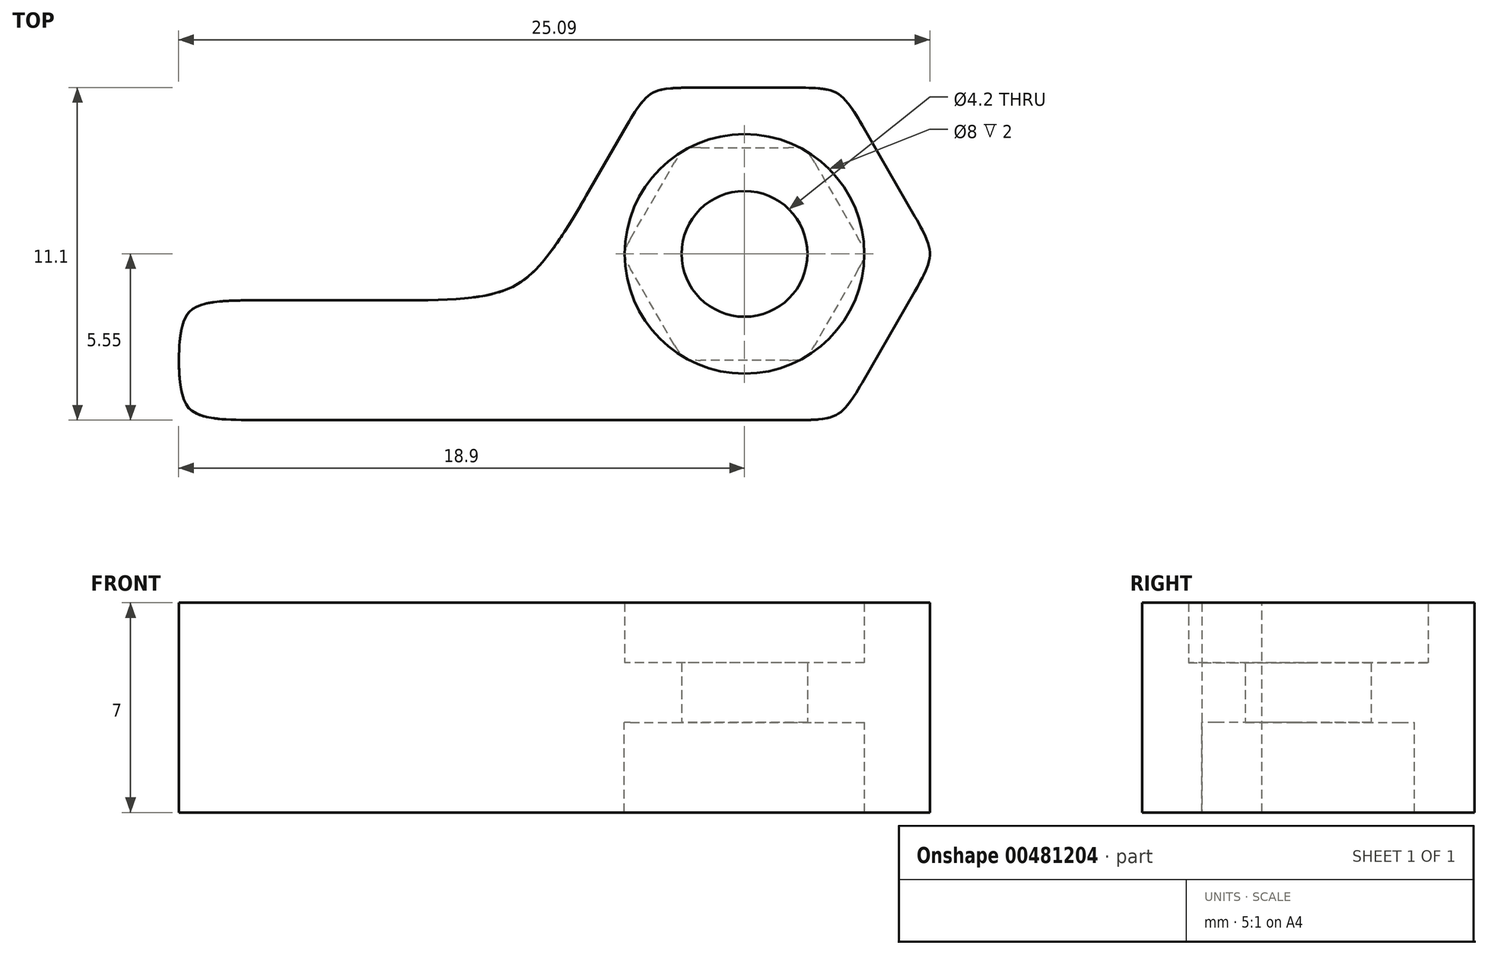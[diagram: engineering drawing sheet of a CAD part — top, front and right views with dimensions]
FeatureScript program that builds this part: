
annotation { "Feature Type Name" : "Feature", "Feature Type Description" : "" }
export const myFeature = defineFeature(function(context is Context, id is Id, definition is map)
    precondition{}
    {
        {
            var Q0;
            Q0=qCreatedBy(makeId("Top.planeOp"),FACE);
            var sketch = newSketch(context, id + "F0", { "sketchPlane" : qUnion([Q0])});
            skCircle(sketch, "E0", {"center": v(0, 0) * mm, "radius": 3.55 * mm, "construction": true});
            skLineSegment(sketch, "E1", {"start": v(-2.05, 3.55) * mm, "end": v(2.05, 3.55) * mm});
            skLineSegment(sketch, "E2", {"start": v(2.05, 3.55) * mm, "end": v(4.1, 0) * mm});
            skLineSegment(sketch, "E3", {"start": v(4.1, 0) * mm, "end": v(2.05, -3.55) * mm});
            skLineSegment(sketch, "E4", {"start": v(2.05, -3.55) * mm, "end": v(-2.05, -3.55) * mm});
            skLineSegment(sketch, "E5", {"start": v(-2.05, -3.55) * mm, "end": v(-4.1, 0) * mm});
            skLineSegment(sketch, "E6", {"start": v(-4.1, 0) * mm, "end": v(-2.05, 3.55) * mm});
            skLineSegment(sketch, "E7.bottom", {"start": v(-18.9, 5.55) * mm, "end": v(7.1, 5.55) * mm});
            skLineSegment(sketch, "E7.top", {"start": v(-18.9, -5.55) * mm, "end": v(7.1, -5.55) * mm});
            skLineSegment(sketch, "E7.left", {"start": v(-18.9, 5.55) * mm, "end": v(-18.9, -5.55) * mm});
            skLineSegment(sketch, "E7.right", {"start": v(7.1, 5.55) * mm, "end": v(7.1, -5.55) * mm});
            skLineSegment(sketch, "E8", {"start": v(0, 3.55) * mm, "end": v(0, 5.55) * mm, "construction": true});
            skLineSegment(sketch, "E9", {"start": v(4.1, 0) * mm, "end": v(7.1, 0) * mm, "construction": true});
            skSolve(sketch);
        }
        {
            var Q0;
            Q0=makeQuery(id+"F0.imprint","IMPRINT",FACE,{"disambiguationData":[TD([[makeQuery(id+"F0.imprint","IMPRINT",EDGE,{"derivedFrom":sQuery(id+"F0.wireOp",EDGE,"E1")}),1.0]])]});
            extrude(context, id + "F1", {"entities" : qUnion([Q0]), "depth" : 3 * mm});
        }
        {
            var Q0;
            Q0=makeQuery(id+"F1.opExtrude","CAP_FACE",FACE,{"disambiguationData":[OSD([sQuery(id+"F0.wireOp",EDGE,"E1"),sQuery(id+"F0.wireOp",EDGE,"E2"),sQuery(id+"F0.wireOp",EDGE,"E3"),sQuery(id+"F0.wireOp",EDGE,"E4"),sQuery(id+"F0.wireOp",EDGE,"E5"),sQuery(id+"F0.wireOp",EDGE,"E6"),sQuery(id+"F0.wireOp",EDGE,"E7.bottom"),sQuery(id+"F0.wireOp",EDGE,"E7.top"),sQuery(id+"F0.wireOp",EDGE,"E7.left"),sQuery(id+"F0.wireOp",EDGE,"E7.right")])],"isStart":false});
            var sketch = newSketch(context, id + "F2", { "sketchPlane" : qUnion([Q0])});
            skLineSegment(sketch, "E10.bottom", {"start": v(-18.9, 5.55) * mm, "end": v(7.1, 5.55) * mm});
            skLineSegment(sketch, "E10.top", {"start": v(-18.9, -5.55) * mm, "end": v(7.1, -5.55) * mm});
            skLineSegment(sketch, "E10.left", {"start": v(-18.9, 5.55) * mm, "end": v(-18.9, -5.55) * mm});
            skLineSegment(sketch, "E10.right", {"start": v(7.1, 5.55) * mm, "end": v(7.1, -5.55) * mm});
            skCircle(sketch, "E11", {"center": v(0, 0) * mm, "radius": 2.1 * mm});
            skSolve(sketch);
        }
        {
            var Q0;
            Q0=qSketchRegion(id+"F2",true);
            extrude(context, id + "F3", {"entities" : qUnion([Q0]), "operationType" : NewBodyOperationType.ADD, "depth" : 2 * mm});
        }
        {
            var Q0;
            Q0=makeQuery(id+"F1.opExtrude","CAP_FACE",FACE,{"disambiguationData":[OSD([sQuery(id+"F0.wireOp",EDGE,"E1"),sQuery(id+"F0.wireOp",EDGE,"E2"),sQuery(id+"F0.wireOp",EDGE,"E3"),sQuery(id+"F0.wireOp",EDGE,"E4"),sQuery(id+"F0.wireOp",EDGE,"E5"),sQuery(id+"F0.wireOp",EDGE,"E6"),sQuery(id+"F0.wireOp",EDGE,"E7.bottom"),sQuery(id+"F0.wireOp",EDGE,"E7.top"),sQuery(id+"F0.wireOp",EDGE,"E7.left"),sQuery(id+"F0.wireOp",EDGE,"E7.right")])],"isStart":true});
            var sketch = newSketch(context, id + "F4", { "sketchPlane" : qUnion([Q0])});
            skLineSegment(sketch, "E12", {"start": v(-3.2, -5.55) * mm, "end": v(-7.3, 1.55) * mm});
            skLineSegment(sketch, "E13", {"start": v(-7.3, 1.55) * mm, "end": v(-18.9, 1.55) * mm});
            skLineSegment(sketch, "E14", {"start": v(-18.9, 1.55) * mm, "end": v(-18.9, -5.55) * mm});
            skLineSegment(sketch, "E15", {"start": v(-18.9, -5.55) * mm, "end": v(-3.2, -5.55) * mm});
            skLineSegment(sketch, "E16", {"start": v(3.2, -5.55) * mm, "end": v(6.4, 0) * mm});
            skLineSegment(sketch, "E17", {"start": v(6.4, 0) * mm, "end": v(3.2, 5.55) * mm});
            skLineSegment(sketch, "E18", {"start": v(3.2, 5.55) * mm, "end": v(7.1, 5.55) * mm});
            skLineSegment(sketch, "E19", {"start": v(7.1, 5.55) * mm, "end": v(7.1, -5.55) * mm});
            skLineSegment(sketch, "E20", {"start": v(7.1, -5.55) * mm, "end": v(3.2, -5.55) * mm});
            skSolve(sketch);
        }
        {
            var Q0;
            Q0=qSketchRegion(id+"F4",true);
            extrude(context, id + "F5", {"entities" : qUnion([Q0]), "operationType" : NewBodyOperationType.REMOVE, "endBound" : BoundingType.UP_TO_NEXT, "oppositeDirection" : true, "depth" : 25 * mm});
        }
        {
            var Q0;
            Q0=makeQuery(id+"F3.opExtrude","CAP_FACE",FACE,{"disambiguationData":[OSD([sQuery(id+"F2.wireOp",EDGE,"E10.bottom"),sQuery(id+"F2.wireOp",EDGE,"E10.top"),sQuery(id+"F2.wireOp",EDGE,"E10.left"),sQuery(id+"F2.wireOp",EDGE,"E10.right"),sQuery(id+"F2.wireOp",EDGE,"E11")])],"isStart":false});
            var sketch = newSketch(context, id + "F6", { "sketchPlane" : qUnion([Q0])});
            skCircle(sketch, "E21", {"center": v(0, 0) * mm, "radius": 4 * mm});
            skSolve(sketch);
        }
        {
            var Q0;
            Q0=makeQuery(id+"F6.imprint","IMPRINT",FACE,{"disambiguationData":[TD([[makeQuery(id+"F6.imprint","IMPRINT",EDGE,{"derivedFrom":sQuery(id+"F6.wireOp",EDGE,"E21")}),-1.0]])]});
            extrude(context, id + "F7", {"entities" : qUnion([Q0]), "operationType" : NewBodyOperationType.ADD, "depth" : 2 * mm});
        }
        {
            var Q0;
            {var subQ0=sQuery(id+"F4.wireOp",EDGE,"E13");var subQ1=sQuery(id+"F4.wireOp",EDGE,"E12");Q0=makeQuery(id+"F7.boolean.opBoolean","MERGE",EDGE,{"derivedFrom":[makeQuery(id+"F5.boolean.opBoolean","COPY",EDGE,{"derivedFrom":makeQuery(id+"F5.opExtrude","SWEPT_EDGE",EDGE,{"disambiguationData":[OSD([subQ1,subQ0])]})}),makeQuery(id+"F7.opExtrude","SWEPT_EDGE",EDGE,{"disambiguationData":[OSD([subQ1,subQ0])]})]});}
            fillet(context, id + "F8", {"entities" : qUnion([Q0]), "radius" : 7 * mm, "tangentPropagation" : true, "rho" : .7, "crossSection" : FilletCrossSection.CONIC, "allowEdgeOverflow" : false});
        }
        {
            var Q0;
            Q0=makeQuery(id+"F8.opFillet","BLEND_EDGE",EDGE,{"blendedFrom":[makeQuery(id+"F5.boolean.opBoolean","COPY",EDGE,{"derivedFrom":makeQuery(id+"F5.opExtrude","SWEPT_EDGE",EDGE,{"disambiguationData":[OSD([sQuery(id+"F4.wireOp",EDGE,"IXpdXx1a-Uic6-cGOW-421j-zm20X8Bzmhcp"),sQuery(id+"F4.wireOp",EDGE,"T3P0GWFI-eLGL-uJRc-1aat-dNIANGRXr7e1")])]})}),makeQuery(id+"F3.boolean.opBoolean","MERGE",FACE,{"derivedFrom":[makeQuery(id+"F1.opExtrude","SWEPT_FACE",FACE,{"disambiguationData":[OSD([sQuery(id+"F0.wireOp",EDGE,"E7.bottom")])]}),makeQuery(id+"F3.opExtrude","SWEPT_FACE",FACE,{"disambiguationData":[OSD([sQuery(id+"F2.wireOp",EDGE,"E10.bottom")])]})]})],"blendedInto":[makeQuery(id+"F3.boolean.opBoolean","MERGE",FACE,{"derivedFrom":[makeQuery(id+"F1.opExtrude","SWEPT_FACE",FACE,{"disambiguationData":[OSD([sQuery(id+"F0.wireOp",EDGE,"E7.bottom")])]}),makeQuery(id+"F3.opExtrude","SWEPT_FACE",FACE,{"disambiguationData":[OSD([sQuery(id+"F2.wireOp",EDGE,"E10.bottom")])]})]})]});
            var Q1;
            Q1=makeQuery(id+"F8.opFillet","BLEND_EDGE",EDGE,{"blendedFrom":[makeQuery(id+"F5.boolean.opBoolean","COPY",EDGE,{"derivedFrom":makeQuery(id+"F5.opExtrude","SWEPT_EDGE",EDGE,{"disambiguationData":[OSD([sQuery(id+"F4.wireOp",EDGE,"jzvlU1Vq-i8A4-SPLi-Q3DD-Y88DfX5X1McG"),sQuery(id+"F4.wireOp",EDGE,"IxcfA2EB-8avC-AsOj-VYOj-H8Ekq08dZs6b")])]})}),makeQuery(id+"F3.boolean.opBoolean","MERGE",FACE,{"derivedFrom":[makeQuery(id+"F1.opExtrude","SWEPT_FACE",FACE,{"disambiguationData":[OSD([sQuery(id+"F0.wireOp",EDGE,"E7.top")])]}),makeQuery(id+"F3.opExtrude","SWEPT_FACE",FACE,{"disambiguationData":[OSD([sQuery(id+"F2.wireOp",EDGE,"E10.top")])]})]})],"blendedInto":[makeQuery(id+"F3.boolean.opBoolean","MERGE",FACE,{"derivedFrom":[makeQuery(id+"F1.opExtrude","SWEPT_FACE",FACE,{"disambiguationData":[OSD([sQuery(id+"F0.wireOp",EDGE,"E7.top")])]}),makeQuery(id+"F3.opExtrude","SWEPT_FACE",FACE,{"disambiguationData":[OSD([sQuery(id+"F2.wireOp",EDGE,"E10.top")])]})]})]});
            var Q2;
            {var subQ0=sQuery(id+"F4.wireOp",EDGE,"E13");Q2=makeQuery(id+"F7.boolean.opBoolean","MERGE",EDGE,{"derivedFrom":[makeQuery(id+"F5.boolean.opBoolean","COPY",EDGE,{"derivedFrom":makeQuery(id+"F5.opExtrude","SWEPT_EDGE",EDGE,{"disambiguationData":[OSD([sQuery(id+"F0.wireOp",EDGE,"E7.left"),subQ0,sQuery(id+"F4.wireOp",EDGE,"E14")])]})}),makeQuery(id+"F7.opExtrude","SWEPT_EDGE",EDGE,{"disambiguationData":[OSD([sQuery(id+"F2.wireOp",EDGE,"E10.left"),subQ0])]})]});}
            var Q3;
            {var subQ0=sQuery(id+"F4.wireOp",EDGE,"E13");Q3=makeQuery(id+"F7.boolean.opBoolean","MERGE",EDGE,{"derivedFrom":[makeQuery(id+"F5.boolean.opBoolean","COPY",EDGE,{"derivedFrom":makeQuery(id+"F5.opExtrude","SWEPT_EDGE",EDGE,{"disambiguationData":[OSD([sQuery(id+"F0.wireOp",EDGE,"E7.left"),subQ0,sQuery(id+"F4.wireOp",EDGE,"E14")])]})}),makeQuery(id+"F7.opExtrude","SWEPT_EDGE",EDGE,{"disambiguationData":[OSD([sQuery(id+"F2.wireOp",EDGE,"E10.left"),subQ0])]})]});}
            var Q4;
            {var subQ0=sQuery(id+"F2.wireOp",EDGE,"E10.left");var subQ1=sQuery(id+"F2.wireOp",EDGE,"E10.top");Q4=makeQuery(id+"F7.boolean.opBoolean","MERGE",EDGE,{"derivedFrom":[makeQuery(id+"F3.boolean.opBoolean","MERGE",EDGE,{"derivedFrom":[makeQuery(id+"F1.opExtrude","SWEPT_EDGE",EDGE,{"disambiguationData":[OSD([sQuery(id+"F0.wireOp",EDGE,"E7.top"),sQuery(id+"F0.wireOp",EDGE,"E7.left")])]}),makeQuery(id+"F3.opExtrude","SWEPT_EDGE",EDGE,{"disambiguationData":[OSD([subQ1,subQ0])]})]}),makeQuery(id+"F7.opExtrude","SWEPT_EDGE",EDGE,{"disambiguationData":[OSD([subQ1,subQ0])]})]});}
            var Q5;
            {var subQ0=sQuery(id+"F4.wireOp",EDGE,"E17");Q5=makeQuery(id+"F7.boolean.opBoolean","MERGE",EDGE,{"derivedFrom":[makeQuery(id+"F5.boolean.opBoolean","COPY",EDGE,{"derivedFrom":makeQuery(id+"F5.opExtrude","SWEPT_EDGE",EDGE,{"disambiguationData":[OSD([sQuery(id+"F0.wireOp",EDGE,"E7.top"),subQ0,sQuery(id+"F4.wireOp",EDGE,"E18")])]})}),makeQuery(id+"F7.opExtrude","SWEPT_EDGE",EDGE,{"disambiguationData":[OSD([sQuery(id+"F2.wireOp",EDGE,"E10.top"),subQ0])]})]});}
            var Q6;
            {var subQ0=sQuery(id+"F4.wireOp",EDGE,"E17");var subQ1=sQuery(id+"F4.wireOp",EDGE,"E16");Q6=makeQuery(id+"F7.boolean.opBoolean","MERGE",EDGE,{"derivedFrom":[makeQuery(id+"F5.boolean.opBoolean","COPY",EDGE,{"derivedFrom":makeQuery(id+"F5.opExtrude","SWEPT_EDGE",EDGE,{"disambiguationData":[OSD([subQ1,subQ0])]})}),makeQuery(id+"F7.opExtrude","SWEPT_EDGE",EDGE,{"disambiguationData":[OSD([subQ1,subQ0])]})]});}
            var Q7;
            {var subQ0=sQuery(id+"F4.wireOp",EDGE,"E16");Q7=makeQuery(id+"F7.boolean.opBoolean","MERGE",EDGE,{"derivedFrom":[makeQuery(id+"F5.boolean.opBoolean","COPY",EDGE,{"derivedFrom":makeQuery(id+"F5.opExtrude","SWEPT_EDGE",EDGE,{"disambiguationData":[OSD([sQuery(id+"F0.wireOp",EDGE,"E7.bottom"),subQ0,sQuery(id+"F4.wireOp",EDGE,"E20")])]})}),makeQuery(id+"F7.opExtrude","SWEPT_EDGE",EDGE,{"disambiguationData":[OSD([sQuery(id+"F2.wireOp",EDGE,"E10.bottom"),subQ0])]})]});}
            var Q8;
            {var subQ0=sQuery(id+"F4.wireOp",EDGE,"E12");Q8=makeQuery(id+"F7.boolean.opBoolean","MERGE",EDGE,{"derivedFrom":[makeQuery(id+"F5.boolean.opBoolean","COPY",EDGE,{"derivedFrom":makeQuery(id+"F5.opExtrude","SWEPT_EDGE",EDGE,{"disambiguationData":[OSD([sQuery(id+"F0.wireOp",EDGE,"E7.bottom"),subQ0,sQuery(id+"F4.wireOp",EDGE,"E15")])]})}),makeQuery(id+"F7.opExtrude","SWEPT_EDGE",EDGE,{"disambiguationData":[OSD([sQuery(id+"F2.wireOp",EDGE,"E10.bottom"),subQ0])]})]});}
            fillet(context, id + "F9", {"entities" : qUnion([Q0, Q1, Q2, Q3, Q4, Q5, Q6, Q7, Q8]), "radius" : 2.5 * mm, "tangentPropagation" : true, "rho" : .7, "crossSection" : FilletCrossSection.CONIC, "allowEdgeOverflow" : false});
        }
        {
            var Q0;
            Q0=makeQuery(id+"F1.opExtrude","SWEPT_EDGE",EDGE,{"disambiguationData":[OSD([sQuery(id+"F0.wireOp",EDGE,"E5"),sQuery(id+"F0.wireOp",EDGE,"E6")])]});
            var Q1;
            Q1=makeQuery(id+"F1.opExtrude","SWEPT_EDGE",EDGE,{"disambiguationData":[OSD([sQuery(id+"F0.wireOp",EDGE,"E1"),sQuery(id+"F0.wireOp",EDGE,"E6")])]});
            var Q2;
            Q2=makeQuery(id+"F1.opExtrude","SWEPT_EDGE",EDGE,{"disambiguationData":[OSD([sQuery(id+"F0.wireOp",EDGE,"E1"),sQuery(id+"F0.wireOp",EDGE,"E2")])]});
            var Q3;
            Q3=makeQuery(id+"F1.opExtrude","SWEPT_EDGE",EDGE,{"disambiguationData":[OSD([sQuery(id+"F0.wireOp",EDGE,"E2"),sQuery(id+"F0.wireOp",EDGE,"E3")])]});
            var Q4;
            Q4=makeQuery(id+"F1.opExtrude","SWEPT_EDGE",EDGE,{"disambiguationData":[OSD([sQuery(id+"F0.wireOp",EDGE,"E3"),sQuery(id+"F0.wireOp",EDGE,"E4")])]});
            var Q5;
            Q5=makeQuery(id+"F1.opExtrude","SWEPT_EDGE",EDGE,{"disambiguationData":[OSD([sQuery(id+"F0.wireOp",EDGE,"E4"),sQuery(id+"F0.wireOp",EDGE,"E5")])]});
            fillet(context, id + "F10", {"entities" : qUnion([Q0, Q1, Q2, Q3, Q4, Q5]), "radius" : 1 * mm, "tangentPropagation" : true, "rho" : .7, "crossSection" : FilletCrossSection.CONIC, "allowEdgeOverflow" : false});
        }
    });
